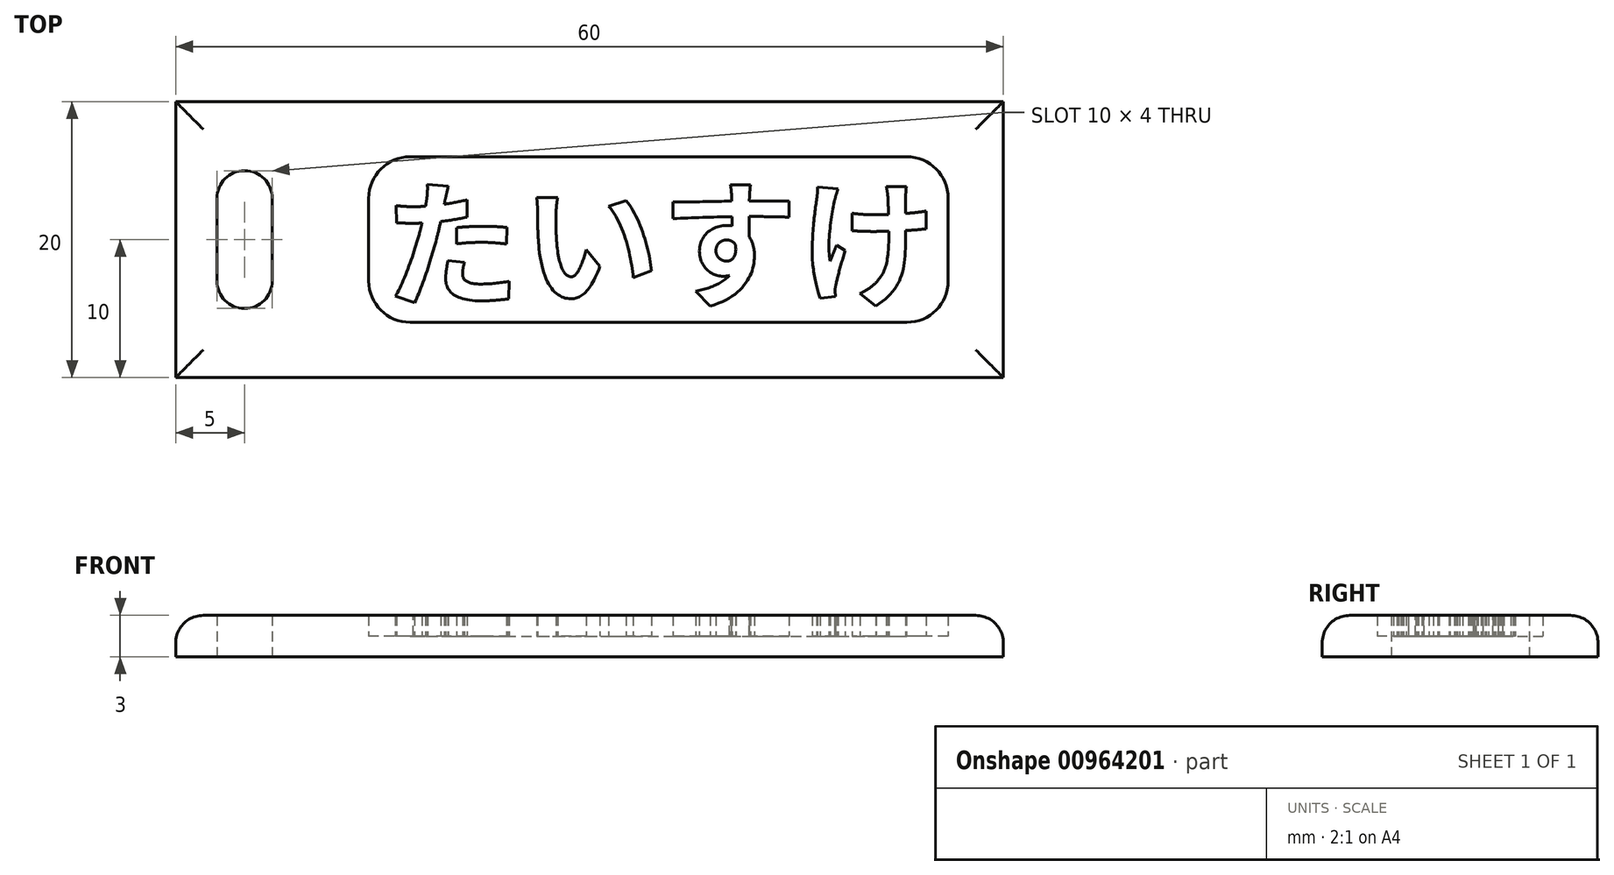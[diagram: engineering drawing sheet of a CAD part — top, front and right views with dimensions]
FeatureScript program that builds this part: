
annotation { "Feature Type Name" : "Feature", "Feature Type Description" : "" }
export const myFeature = defineFeature(function(context is Context, id is Id, definition is map)
    precondition{}
    {
        {
            var Q0;
            Q0=qCreatedBy(makeId("Top.planeOp"),FACE);
            var sketch = newSketch(context, id + "F0", { "sketchPlane" : qUnion([Q0])});
            skLineSegment(sketch, "E0.bottom", {"start": v(-25, 10) * mm, "end": v(25, 10) * mm});
            skLineSegment(sketch, "E0.top", {"start": v(-25, -10) * mm, "end": v(25, -10) * mm});
            skLineSegment(sketch, "E0.left", {"start": v(-25, 10) * mm, "end": v(-25, -10) * mm});
            skLineSegment(sketch, "E0.right", {"start": v(25, 10) * mm, "end": v(25, -10) * mm});
            skPoint(sketch, "E0.middle", {"position": v(0, 0) * mm});
            skLineSegment(sketch, "E1.bottom", {"start": v(-25, 10) * mm, "end": v(-35, 10) * mm});
            skLineSegment(sketch, "E1.top", {"start": v(-25, -10) * mm, "end": v(-35, -10) * mm});
            skLineSegment(sketch, "E1.right", {"start": v(-35, 10) * mm, "end": v(-35, -10) * mm});
            skPoint(sketch, "E1.middle", {"position": v(-30, 0) * mm});
            skPoint(sketch, "E1.middle.positionSnap0", {"position": v(-25, 0) * mm});
            skPoint(sketch, "E1.centerSnap0", {"position": v(-25, 0) * mm});
            skLineSegment(sketch, "E2.bottom", {"start": v(-30, 5) * mm, "end": v(-30, 5) * mm});
            skLineSegment(sketch, "E2.top", {"start": v(-30, -5) * mm, "end": v(-30, -5) * mm});
            skLineSegment(sketch, "E2.left", {"start": v(-32, 3) * mm, "end": v(-32, -3) * mm});
            skLineSegment(sketch, "E2.right", {"start": v(-28, 3) * mm, "end": v(-28, -3) * mm});
            skPoint(sketch, "E3.visualSharp", {"position": v(-32, 5) * mm});
            skArc(sketch, "E3.filletArc", {"start": v(-30, 5) * mm, "mid": v(-31.41, 4.41) * mm, "end": v(-32, 3) * mm});
            skPoint(sketch, "E4.visualSharp", {"position": v(-28, 5) * mm});
            skArc(sketch, "E4.filletArc", {"start": v(-28, 3) * mm, "mid": v(-28.59, 4.41) * mm, "end": v(-30, 5) * mm});
            skPoint(sketch, "E5.visualSharp", {"position": v(-28, -5) * mm});
            skArc(sketch, "E5.filletArc", {"start": v(-30, -5) * mm, "mid": v(-28.59, -4.41) * mm, "end": v(-28, -3) * mm});
            skPoint(sketch, "E6.visualSharp", {"position": v(-32, -5) * mm});
            skArc(sketch, "E6.filletArc", {"start": v(-32, -3) * mm, "mid": v(-31.41, -4.41) * mm, "end": v(-30, -5) * mm});
            skSolve(sketch);
        }
        {
            var Q0;
            Q0 = qSketchRegion(id + "F0", true);
            extrude(context, id + "F1", {"entities" : qUnion([Q0]), "depth" : 3 * mm, "offsetDistance" : 25 * mm});
        }
        {
            var Q0;
            Q0=qCreatedBy(makeId("Top.planeOp"),FACE);
            var sketch = newSketch(context, id + "F2", { "sketchPlane" : qUnion([Q0])});
            skLineSegment(sketch, "E7.bottom", {"start": v(-18, 6) * mm, "end": v(18, 6) * mm});
            skLineSegment(sketch, "E7.top", {"start": v(-18, -6) * mm, "end": v(18, -6) * mm});
            skLineSegment(sketch, "E7.left", {"start": v(-21, 3) * mm, "end": v(-21, -3) * mm});
            skLineSegment(sketch, "E7.right", {"start": v(21, 3) * mm, "end": v(21, -3) * mm});
            skPoint(sketch, "E7.middle", {"position": v(0, 0) * mm});
            skPoint(sketch, "E8.visualSharp", {"position": v(-21, 6) * mm});
            skArc(sketch, "E8.filletArc", {"start": v(-18, 6) * mm, "mid": v(-20.12, 5.12) * mm, "end": v(-21, 3) * mm});
            skPoint(sketch, "E9.visualSharp", {"position": v(21, 6) * mm});
            skArc(sketch, "E9.filletArc", {"start": v(21, 3) * mm, "mid": v(20.12, 5.12) * mm, "end": v(18, 6) * mm});
            skPoint(sketch, "E10.visualSharp", {"position": v(21, -6) * mm});
            skArc(sketch, "E10.filletArc", {"start": v(18, -6) * mm, "mid": v(20.12, -5.12) * mm, "end": v(21, -3) * mm});
            skPoint(sketch, "E11.visualSharp", {"position": v(-21, -6) * mm});
            skArc(sketch, "E11.filletArc", {"start": v(-21, -3) * mm, "mid": v(-20.12, -5.12) * mm, "end": v(-18, -6) * mm});
            skSolve(sketch);
        }
        {
            var Q0;
            Q0 = qSketchRegion(id + "F2", true);
            extrude(context, id + "F3", {"entities" : qUnion([Q0]), "depth" : 3 * mm, "offsetDistance" : 25 * mm});
        }
        {
            var Q0;
            Q0=makeQuery(id+"F3.opExtrude","SWEPT_BODY",BODY,{"disambiguationData":[OSD([sQuery(id+"F2.wireOp",EDGE,"E7.bottom"),sQuery(id+"F2.wireOp",EDGE,"E7.top"),sQuery(id+"F2.wireOp",EDGE,"E7.left"),sQuery(id+"F2.wireOp",EDGE,"E7.right"),sQuery(id+"F2.wireOp",EDGE,"E8.filletArc"),sQuery(id+"F2.wireOp",EDGE,"E9.filletArc"),sQuery(id+"F2.wireOp",EDGE,"E10.filletArc"),sQuery(id+"F2.wireOp",EDGE,"E11.filletArc")])]});
            transform(context, id + "F4", {"entities" : qUnion([Q0]), "transformType" : TransformType.TRANSLATION_3D, "dx" : 0 * mm, "dy" : 0 * mm, "dz" : 1.5 * mm, "makeCopy" : false});
        }
        {
            var Q0;
            Q0=makeQuery(id+"F3.opExtrude","SWEPT_BODY",BODY,{"disambiguationData":[OSD([sQuery(id+"F2.wireOp",EDGE,"E7.bottom"),sQuery(id+"F2.wireOp",EDGE,"E7.top"),sQuery(id+"F2.wireOp",EDGE,"E7.left"),sQuery(id+"F2.wireOp",EDGE,"E7.right"),sQuery(id+"F2.wireOp",EDGE,"E8.filletArc"),sQuery(id+"F2.wireOp",EDGE,"E9.filletArc"),sQuery(id+"F2.wireOp",EDGE,"E10.filletArc"),sQuery(id+"F2.wireOp",EDGE,"E11.filletArc")])]});
            var Q1;
            Q1=makeQuery(id+"F1.opExtrude","SWEPT_BODY",BODY,{"disambiguationData":[OSD([sQuery(id+"F0.wireOp",EDGE,"E0.bottom"),sQuery(id+"F0.wireOp",EDGE,"E0.top"),sQuery(id+"F0.wireOp",EDGE,"E0.right"),sQuery(id+"F0.wireOp",EDGE,"E1.bottom"),sQuery(id+"F0.wireOp",EDGE,"E1.top"),sQuery(id+"F0.wireOp",EDGE,"E1.right"),sQuery(id+"F0.wireOp",EDGE,"E2.left"),sQuery(id+"F0.wireOp",EDGE,"E2.right"),sQuery(id+"F0.wireOp",EDGE,"E3.filletArc"),sQuery(id+"F0.wireOp",EDGE,"E4.filletArc"),sQuery(id+"F0.wireOp",EDGE,"E5.filletArc"),sQuery(id+"F0.wireOp",EDGE,"E6.filletArc")])]});
            booleanBodies(context, id + "F5", {"operationType" : BooleanOperationType.SUBTRACTION, "tools" : qUnion([Q0]), "targets" : qUnion([Q1])});
        }
        {
            var Q0;
            Q0=qCreatedBy(makeId("Top.planeOp"),FACE);
            var sketch = newSketch(context, id + "F6", { "sketchPlane" : qUnion([Q0])});
            skText(sketch, "E12", { "text": "たいすけ", "fontName": "NotoSansCJKjp-Bold.otf"});
            const initialGuessF6  = {"E12": [-0.02, -0.00412, 1, 0, 0.00724]};
            skSetInitialGuess(sketch, initialGuessF6);
            skSolve(sketch);
        }
        {
            var Q0;
            Q0 = qSketchRegion(id + "F6", true);
            extrude(context, id + "F7", {"entities" : qUnion([Q0]), "operationType" : NewBodyOperationType.ADD, "depth" : 3 * mm, "offsetDistance" : 25 * mm});
        }
        {
            var Q0;
            Q0=makeQuery(id+"F1.opExtrude","CAP_EDGE",EDGE,{"disambiguationData":[OSD([sQuery(id+"F0.wireOp",EDGE,"E0.bottom"),sQuery(id+"F0.wireOp",EDGE,"E1.bottom")])],"isStart":false});
            var Q1;
            Q1=makeQuery(id+"F1.opExtrude","CAP_EDGE",EDGE,{"disambiguationData":[OSD([sQuery(id+"F0.wireOp",EDGE,"E1.right")])],"isStart":false});
            var Q2;
            Q2=makeQuery(id+"F1.opExtrude","CAP_EDGE",EDGE,{"disambiguationData":[OSD([sQuery(id+"F0.wireOp",EDGE,"E0.top"),sQuery(id+"F0.wireOp",EDGE,"E1.top")])],"isStart":false});
            var Q3;
            Q3=makeQuery(id+"F1.opExtrude","CAP_EDGE",EDGE,{"disambiguationData":[OSD([sQuery(id+"F0.wireOp",EDGE,"E0.right")])],"isStart":false});
            fillet(context, id + "F8", {"entities" : qUnion([Q0, Q1, Q2, Q3]), "radius" : 2 * mm, "tangentPropagation" : true, "allowEdgeOverflow" : false});
        }
    });
